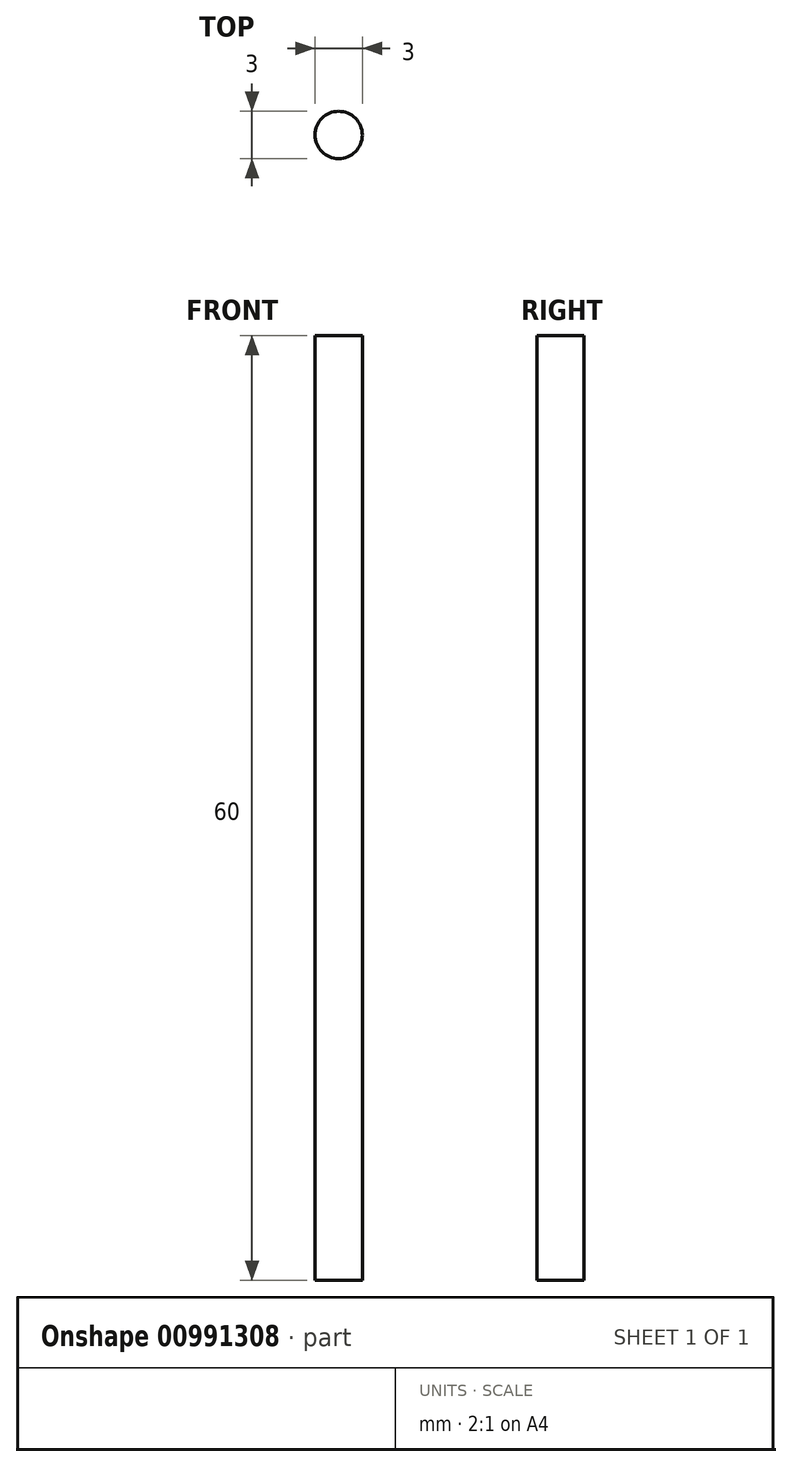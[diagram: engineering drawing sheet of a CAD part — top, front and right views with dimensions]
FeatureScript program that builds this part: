
annotation { "Feature Type Name" : "Feature", "Feature Type Description" : "" }
export const myFeature = defineFeature(function(context is Context, id is Id, definition is map)
    precondition{}
    {
        {
            var Q0;
            Q0=qCreatedBy(makeId("Top.planeOp"),FACE);
            var sketch = newSketch(context, id + "F0", { "sketchPlane" : qUnion([Q0])});
            skCircle(sketch, "E0", {"center": v(0, 0) * mm, "radius": 1.5 * mm});
            skSolve(sketch);
        }
        {
            var Q0;
            Q0=qSketchRegion(id+"F0",true);
            extrude(context, id + "F1", {"entities" : qUnion([Q0]), "depth" : 60 * mm, "offsetDistance" : 25 * mm});
        }
    });
